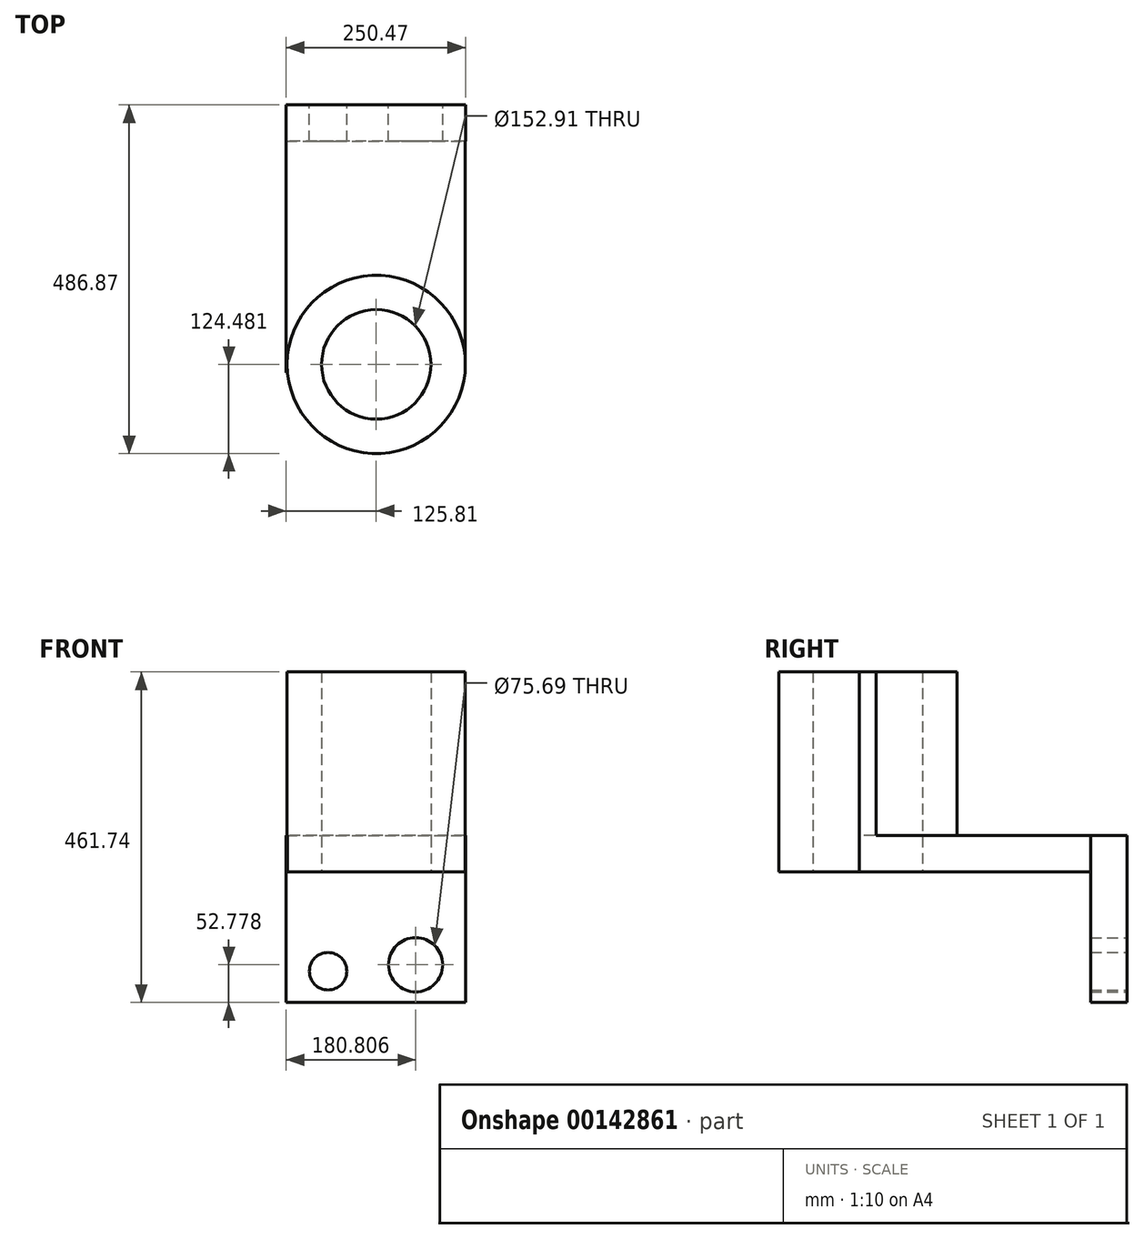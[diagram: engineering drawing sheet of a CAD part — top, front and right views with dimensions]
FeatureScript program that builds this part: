
annotation { "Feature Type Name" : "Feature", "Feature Type Description" : "" }
export const myFeature = defineFeature(function(context is Context, id is Id, definition is map)
    precondition{}
    {
        {
            var Q0;
            Q0=qCreatedBy(makeId("Top.planeOp"),FACE);
            var sketch = newSketch(context, id + "F0", { "sketchPlane" : qUnion([Q0])});
            skCircle(sketch, "E0", {"center": v(0, 0) * mm, "radius": 12.77 * mm});
            skCircle(sketch, "E1", {"center": v(0, 38.93) * mm, "radius": 124.49 * mm});
            skCircle(sketch, "E2", {"center": v(0, 38.93) * mm, "radius": 76.46 * mm});
            skLineSegment(sketch, "E3.bottom", {"start": v(123.95, 27.38) * mm, "end": v(-125.8, 27.38) * mm});
            skLineSegment(sketch, "E3.top", {"start": v(123.95, 350.52) * mm, "end": v(-125.8, 350.52) * mm});
            skLineSegment(sketch, "E3.left", {"start": v(123.95, 27.38) * mm, "end": v(123.95, 350.52) * mm});
            skLineSegment(sketch, "E3.right", {"start": v(-125.8, 27.38) * mm, "end": v(-125.8, 350.52) * mm});
            skSolve(sketch);
        }
        {
            var Q0;
            {var subQ0=sQuery(id+"F0.wireOp",EDGE,"E3.bottom");var subQ1=sQuery(id+"F0.wireOp",EDGE,"E1");var subQ2=makeQuery(id+"F0.imprint","INTERSECT",VERTEX,{"derivedFrom":[subQ1,subQ0]});Q0=makeQuery(id+"F0.imprint","IMPRINT",FACE,{"disambiguationData":[TD([[makeQuery(id+"F0.imprint","IMPRINT",EDGE,{"disambiguationData":[TD([[subQ2,1.0]])],"derivedFrom":subQ1}),1.0]])]});}
            var Q1;
            {var subQ0=sQuery(id+"F0.wireOp",EDGE,"E3.bottom");var subQ4=sQuery(id+"F0.wireOp",EDGE,"E2");var subQ5=makeQuery(id+"F0.imprint","INTERSECT",VERTEX,{"disambiguationData":[OD(0.0)],"derivedFrom":[subQ4,subQ0]});Q1=makeQuery(id+"F0.imprint","IMPRINT",FACE,{"disambiguationData":[TD([[makeQuery(id+"F0.imprint","IMPRINT",EDGE,{"disambiguationData":[TD([[subQ5,1.0]])],"derivedFrom":subQ4}),-1.0]])]});}
            extrude(context, id + "F6", {"entities" : qUnion([Q0, Q1]), "depth" : 25.4 * mm});
        }
        {
            var Q0;
            Q0=makeQuery(id+"F6.opExtrude","CAP_FACE",FACE,{"disambiguationData":[OSD([sQuery(id+"F0.wireOp",EDGE,"E1"),sQuery(id+"F0.wireOp",EDGE,"E2"),sQuery(id+"F0.wireOp",EDGE,"E3.left")])],"isStart":false});
            extrude(context, id + "F1", {"entities" : qUnion([Q0]), "operationType" : NewBodyOperationType.ADD, "depth" : 254 * mm});
        }
        {
            var Q0;
            {var subQ1=sQuery(id+"F0.wireOp",EDGE,"E3.top");Q0=makeQuery(id+"F0.imprint","IMPRINT",FACE,{"disambiguationData":[TD([[makeQuery(id+"F0.imprint","IMPRINT",EDGE,{"derivedFrom":subQ1}),1.0]])]});}
            extrude(context, id + "F7", {"entities" : qUnion([Q0]), "operationType" : NewBodyOperationType.ADD, "depth" : 50.8 * mm});
        }
        {
            var Q0;
            Q0=makeQuery(id+"F7.opExtrude","SWEPT_FACE",FACE,{"disambiguationData":[OSD([sQuery(id+"F0.wireOp",EDGE,"E3.top")])]});
            var sketch = newSketch(context, id + "F8", { "sketchPlane" : qUnion([Q0])});
            skLineSegment(sketch, "E4.bottom", {"start": v(125.8, 50.8) * mm, "end": v(-124.66, 50.8) * mm});
            skLineSegment(sketch, "E4.top", {"start": v(125.8, -182.34) * mm, "end": v(-124.66, -182.34) * mm});
            skLineSegment(sketch, "E4.left", {"start": v(125.8, 50.8) * mm, "end": v(125.8, -182.34) * mm});
            skLineSegment(sketch, "E4.right", {"start": v(-124.66, 50.8) * mm, "end": v(-124.66, -182.34) * mm});
            skSolve(sketch);
        }
        {
            var Q0;
            {var subQ0=sQuery(id+"F8.wireOp",EDGE,"E4.top");Q0=makeQuery(id+"F8.imprint","IMPRINT",FACE,{"disambiguationData":[TD([[makeQuery(id+"F8.imprint","IMPRINT",EDGE,{"derivedFrom":subQ0}),-1.0]])]});}
            var Q1;
            {var subQ1=sQuery(id+"F0.wireOp",EDGE,"E3.top");var subQ5=makeQuery(id+"F7.opExtrude","CAP_EDGE",EDGE,{"disambiguationData":[OSD([subQ1])],"isStart":true});Q1=makeQuery(id+"F8.imprint","IMPRINT",FACE,{"disambiguationData":[TD([[makeQuery(id+"F8.imprint","IMPRINT",EDGE,{"derivedFrom":subQ5}),1.0]])]});}
            extrude(context, id + "F2", {"entities" : qUnion([Q0, Q1]), "operationType" : NewBodyOperationType.ADD, "depth" : 50.8 * mm});
        }
        {
            var Q0;
            Q0=makeQuery(id+"F2.opExtrude","CAP_FACE",FACE,{"disambiguationData":[OSD([sQuery(id+"F8.wireOp",EDGE,"E4.bottom"),sQuery(id+"F8.wireOp",EDGE,"E4.top"),sQuery(id+"F8.wireOp",EDGE,"E4.left"),sQuery(id+"F8.wireOp",EDGE,"E4.right")])],"isStart":false});
            var sketch = newSketch(context, id + "F9", { "sketchPlane" : qUnion([Q0])});
            skCircle(sketch, "E5", {"center": v(67.32, -138.6) * mm, "radius": 26.12 * mm});
            skCircle(sketch, "E6", {"center": v(-68.7, -144.1) * mm, "radius": 29.44 * mm});
            skSolve(sketch);
        }
        {
            var Q0;
            Q0=makeQuery(id+"F9.imprint","IMPRINT",FACE,{"disambiguationData":[TD([[makeQuery(id+"F9.imprint","IMPRINT",EDGE,{"derivedFrom":sQuery(id+"F9.wireOp",EDGE,"E5")}),1.0]])]});
            extrude(context, id + "F10", {"entities" : qUnion([Q0]), "operationType" : NewBodyOperationType.REMOVE, "oppositeDirection" : true, "depth" : 25.4 * mm});
        }
        {
            var Q0;
            Q0=makeQuery(id+"F10.boolean.opBoolean","COPY",FACE,{"derivedFrom":makeQuery(id+"F10.opExtrude","CAP_FACE",FACE,{"disambiguationData":[OSD([sQuery(id+"F9.wireOp",EDGE,"E5")])],"isStart":false})});
            extrude(context, id + "F11", {"entities" : qUnion([Q0]), "operationType" : NewBodyOperationType.REMOVE, "oppositeDirection" : true, "depth" : 25.4 * mm});
        }
        {
            var Q0;
            Q0=makeQuery(id+"F2.opExtrude","CAP_FACE",FACE,{"disambiguationData":[OSD([sQuery(id+"F8.wireOp",EDGE,"E4.bottom"),sQuery(id+"F8.wireOp",EDGE,"E4.top"),sQuery(id+"F8.wireOp",EDGE,"E4.left"),sQuery(id+"F8.wireOp",EDGE,"E4.right")])],"isStart":false});
            var sketch = newSketch(context, id + "F3", { "sketchPlane" : qUnion([Q0])});
            skCircle(sketch, "E7", {"center": v(-55, -129.56) * mm, "radius": 37.85 * mm});
            skSolve(sketch);
        }
        {
            var Q0;
            Q0=makeQuery(id+"F3.imprint","IMPRINT",FACE,{"disambiguationData":[TD([[makeQuery(id+"F3.imprint","IMPRINT",EDGE,{"derivedFrom":sQuery(id+"F3.wireOp",EDGE,"E7")}),1.0]])]});
            extrude(context, id + "F4", {"entities" : qUnion([Q0]), "operationType" : NewBodyOperationType.REMOVE, "oppositeDirection" : true, "depth" : 558.8 * mm});
        }
    });
